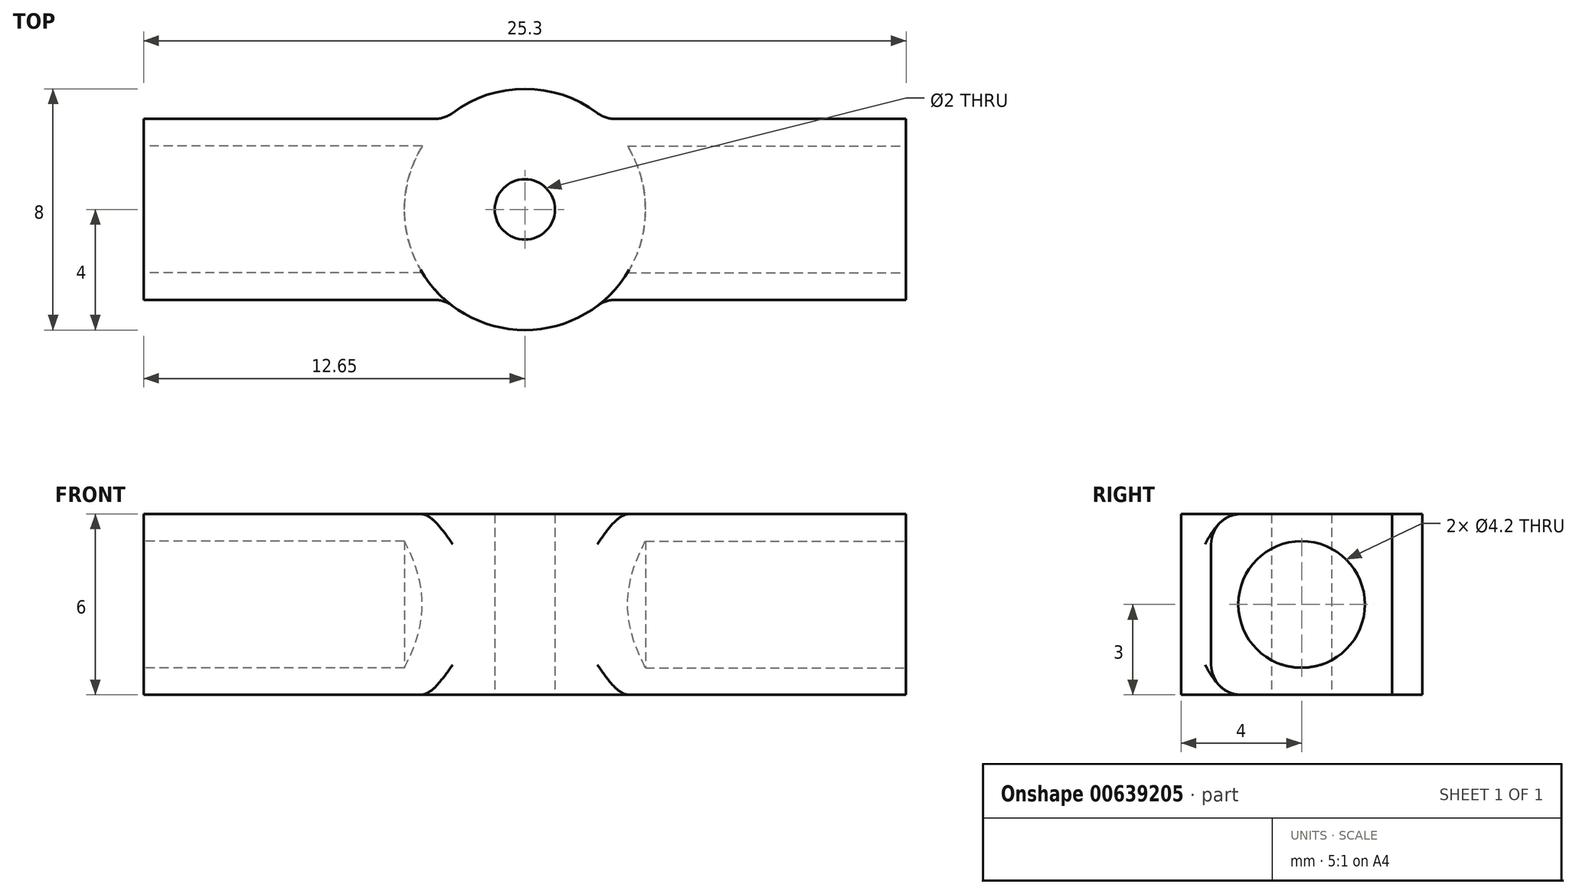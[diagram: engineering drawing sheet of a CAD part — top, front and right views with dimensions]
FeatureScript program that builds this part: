
annotation { "Feature Type Name" : "Feature", "Feature Type Description" : "" }
export const myFeature = defineFeature(function(context is Context, id is Id, definition is map)
    precondition{}
    {
        {
            var Q0;
            Q0=qCreatedBy(makeId("Top.planeOp"),FACE);
            var sketch = newSketch(context, id + "F0", { "sketchPlane" : qUnion([Q0])});
            skCircle(sketch, "E0", {"center": v(0, 0) * mm, "radius": 1 * mm});
            skArc(sketch, "E1.0", {"start": v(2.65, 3) * mm, "mid": v(-4, 0) * mm, "end": v(2.65, -3) * mm});
            skLineSegment(sketch, "E2", {"start": v(2.65, -3) * mm, "end": v(12.65, -3) * mm});
            skLineSegment(sketch, "E3", {"start": v(12.65, -3) * mm, "end": v(12.65, 3) * mm});
            skLineSegment(sketch, "E4", {"start": v(12.65, 3) * mm, "end": v(2.65, 3) * mm});
            skSolve(sketch);
        }
        {
            var Q0;
            Q0=qSketchRegion(id+"F0",true);
            extrude(context, id + "F1", {"entities" : qUnion([Q0]), "depth" : 6 * mm, "offsetDistance" : 25 * mm});
        }
        {
            var Q0;
            Q0=makeQuery(id+"F1.opExtrude","SWEPT_FACE",FACE,{"disambiguationData":[OSD([sQuery(id+"F0.wireOp",EDGE,"E3")])]});
            var sketch = newSketch(context, id + "F2", { "sketchPlane" : qUnion([Q0])});
            skCircle(sketch, "E5", {"center": v(0, 3) * mm, "radius": 2.1 * mm});
            skLineSegment(sketch, "E6", {"start": v(0, 0) * mm, "end": v(0, 6) * mm, "construction": true});
            skSolve(sketch);
        }
        {
            var Q0;
            Q0=qSketchRegion(id+"F2",true);
            extrude(context, id + "F3", {"entities" : qUnion([Q0]), "operationType" : NewBodyOperationType.REMOVE, "oppositeDirection" : true, "depth" : 10 * mm, "offsetDistance" : 25 * mm});
        }
        {
            var Q0;
            Q0=makeQuery(id+"F1.opExtrude","SWEPT_EDGE",EDGE,{"disambiguationData":[OSD([sQuery(id+"F0.wireOp",EDGE,"E1.0"),sQuery(id+"F0.wireOp",EDGE,"E4")])]});
            var Q1;
            Q1=makeQuery(id+"F1.opExtrude","SWEPT_EDGE",EDGE,{"disambiguationData":[OSD([sQuery(id+"F0.wireOp",EDGE,"E1.0"),sQuery(id+"F0.wireOp",EDGE,"E2")])]});
            var Q2;
            Q2=makeQuery(id+"F1.opExtrude","CAP_EDGE",EDGE,{"disambiguationData":[OSD([sQuery(id+"F0.wireOp",EDGE,"E2")])],"isStart":false});
            var Q3;
            Q3=makeQuery(id+"F1.opExtrude","CAP_EDGE",EDGE,{"disambiguationData":[OSD([sQuery(id+"F0.wireOp",EDGE,"E2")])],"isStart":true});
            fillet(context, id + "F4", {"entities" : qUnion([Q0, Q1, Q2, Q3]), "radius" : 1 * mm, "tangentPropagation" : true, "allowEdgeOverflow" : false});
        }
        {
            var Q0;
            Q0=makeQuery(id+"F1.opExtrude","SWEPT_BODY",BODY,{"disambiguationData":[OSD([sQuery(id+"F0.wireOp",EDGE,"E0"),sQuery(id+"F0.wireOp",EDGE,"E1.0"),sQuery(id+"F0.wireOp",EDGE,"E2"),sQuery(id+"F0.wireOp",EDGE,"E3"),sQuery(id+"F0.wireOp",EDGE,"E4")])]});
            var Q1;
            Q1=qCreatedBy(makeId("Right.planeOp"),FACE);
            mirror(context, id + "F5", {"operationType" : NewBodyOperationType.ADD, "entities" : qUnion([Q0]), "mirrorPlane" : qUnion([Q1])});
        }
    });
